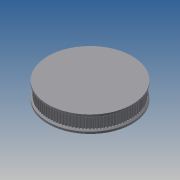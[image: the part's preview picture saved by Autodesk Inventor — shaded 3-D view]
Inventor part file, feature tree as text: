
AUTODESK INVENTOR PART (.ipt)
format: ipt  version: 2013 (Build 170138000, 138)  size: 1,191,936 bytes
history: native  units: mm
features: extrude x5, sketch x5, pattern_circular x1, chamfer x1, mirror x1
ambient origin geometry x8: Origin, YZ Plane, XZ Plane, XY Plane, X Axis, Y Axis, Z Axis, Center Point
bodies: Solid1 (feature_tree)
feature tree (13):
  extrude  "Extrusion1"  Depth=0.628319mm
  pattern_circular  "Circular Pattern1"  [2 undecoded]
  extrude  "Extrusion3"  Depth=0.75mm
  chamfer  "Chamfer2"  Distance=0.254mm
  mirror  "Mirror1"
  extrude  "Extrusion4"  Depth=8.0mm TaperAngle=0.0deg
  extrude  "Extrusion5"  Depth=1000.0mm
  extrude  "Extrusion6"  TaperAngle=360.0deg  [1 undecoded]
  sketch  "Sketch1"  dims[d0=63.661977mm d9=0.628319mm]
  sketch  "Sketch3"  dims[d11=0.254mm]
  sketch  "Sketch4"  dims[d12=0.3mm]
  sketch  "Sketch5"  dims[d13=0.4mm]
  sketch  "Sketch6"  dims[d14=1.0mm d15=0.555mm d16=0.75mm d17=0.254mm d18=8.0mm d19=0.0mm d20=1000.0mm d21=360.0deg d23=0.1mm d32=2.5mm d33=0.0mm d34=1.0mm d35=2.0mm d36=45.0deg d37=15.0mm d39=3.5mm d40=15.0mm d41=25.0mm d42=2.0mm d43=0.0mm d44=6.0mm d46=3.0mm d47=0.0mm d49=22.0mm d51=7.0mm d52=0.0mm d53=1.0mm]
note: 3 required parameter values undecoded (feature->parameter linkage not recoverable at this tier; creation-order binding heuristic only, values carry confidence <= 0.55)
